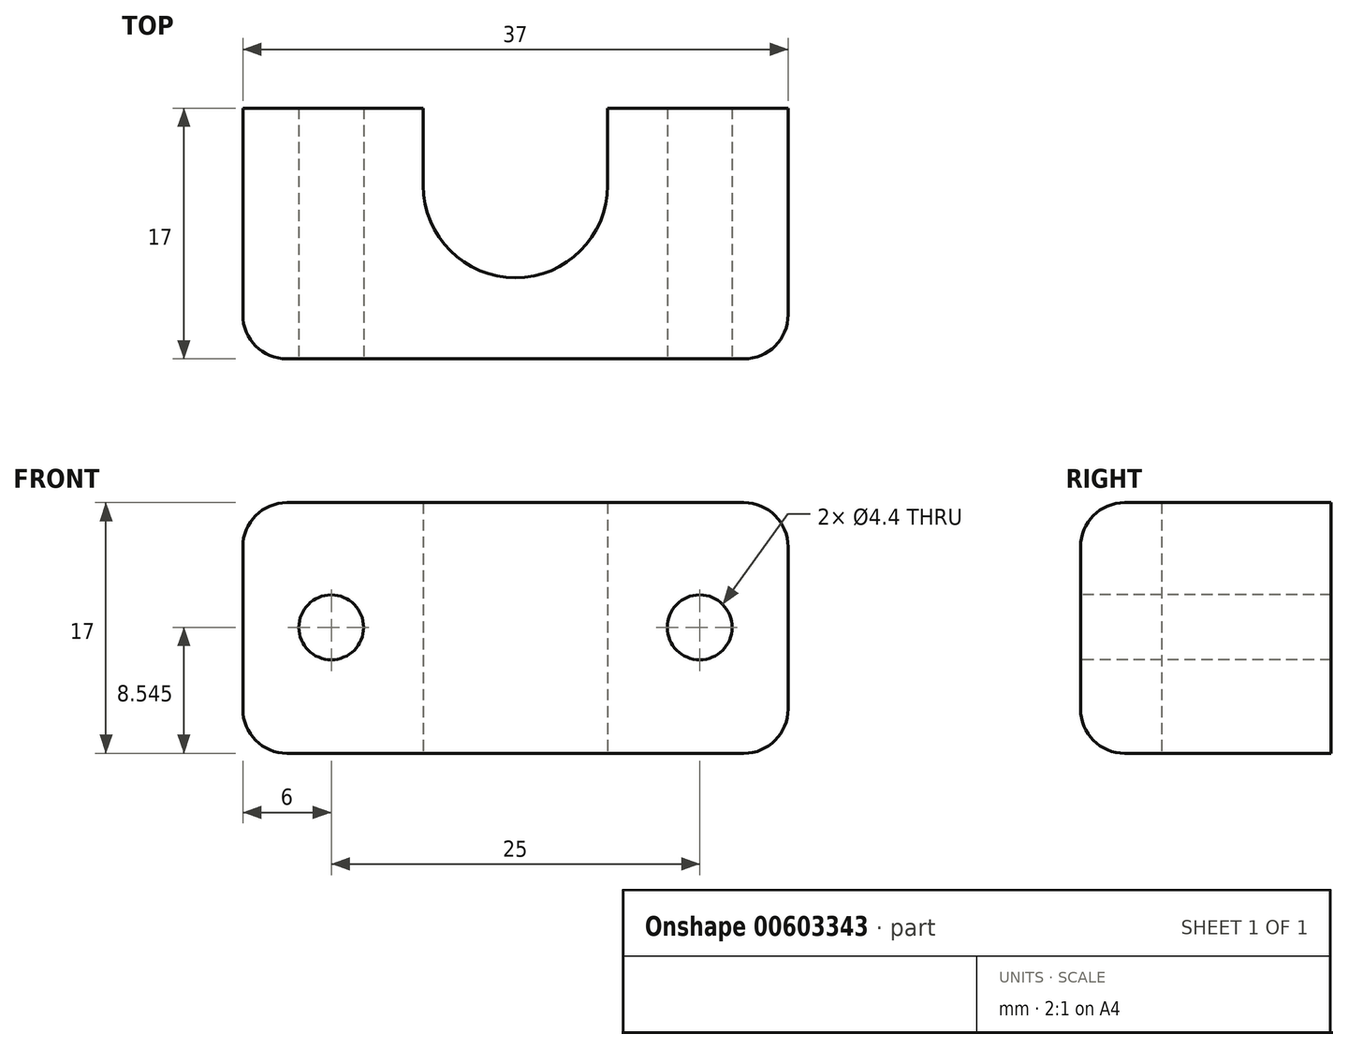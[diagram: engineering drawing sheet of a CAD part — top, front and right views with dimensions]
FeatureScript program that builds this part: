
annotation { "Feature Type Name" : "Feature", "Feature Type Description" : "" }
export const myFeature = defineFeature(function(context is Context, id is Id, definition is map)
    precondition{}
    {
        {
            var Q0;
            Q0=qCreatedBy(makeId("Top.planeOp"),FACE);
            var sketch = newSketch(context, id + "F0", { "sketchPlane" : qUnion([Q0])});
            skLineSegment(sketch, "E0.bottom", {"start": v(0, 0) * mm, "end": v(-37, 0) * mm});
            skLineSegment(sketch, "E0.top", {"start": v(0, 17) * mm, "end": v(-37, 17) * mm});
            skLineSegment(sketch, "E0.left", {"start": v(0, 0) * mm, "end": v(0, 17) * mm});
            skLineSegment(sketch, "E0.right", {"start": v(-37, 0) * mm, "end": v(-37, 17) * mm});
            skCircle(sketch, "E1", {"center": v(-18.5, 11.75) * mm, "radius": 6.25 * mm});
            skLineSegment(sketch, "E2", {"start": v(-18.5, 17) * mm, "end": v(-18.5, 0) * mm, "construction": true});
            skLineSegment(sketch, "E3", {"start": v(-24.75, 11.75) * mm, "end": v(-24.75, 17) * mm});
            skLineSegment(sketch, "E4.MirrorCS", {"start": v(-12.25, 11.75) * mm, "end": v(-12.25, 17) * mm});
            skSolve(sketch);
        }
        {
            var Q0;
            Q0=makeQuery(id+"F0.imprint","IMPRINT",FACE,{"disambiguationData":[TD([[makeQuery(id+"F0.imprint","IMPRINT",EDGE,{"derivedFrom":sQuery(id+"F0.wireOp",EDGE,"E0.bottom")}),-1.0]])]});
            extrude(context, id + "F1", {"entities" : qUnion([Q0]), "depth" : 17 * mm, "offsetDistance" : 25 * mm});
        }
        {
            var Q0;
            Q0=makeQuery(id+"F1.opExtrude","SWEPT_FACE",FACE,{"disambiguationData":[OSD([sQuery(id+"F0.wireOp",EDGE,"E0.bottom")])]});
            var sketch = newSketch(context, id + "F2", { "sketchPlane" : qUnion([Q0])});
            skPoint(sketch, "E5", {"position": v(-6, 8.54) * mm});
            skLineSegment(sketch, "E6", {"start": v(-24.7, 8.68) * mm, "end": v(0, 8.5) * mm, "construction": true});
            skLineSegment(sketch, "E7", {"start": v(-18.5, 17) * mm, "end": v(-18.5, 7.59) * mm, "construction": true});
            skPoint(sketch, "E8.MirrorP", {"position": v(-31, 8.54) * mm});
            skSolve(sketch);
        }
        {
            var Q0;
            Q0=sQuery(id+"F2.wireOp",VERTEX,"E8.MirrorP");
            var Q1;
            Q1=sQuery(id+"F2.wireOp",VERTEX,"E5");
            var Q2;
            Q2=makeQuery(id+"F1.opExtrude","SWEPT_BODY",BODY,{"disambiguationData":[OSD([sQuery(id+"F0.wireOp",EDGE,"E0.bottom"),sQuery(id+"F0.wireOp",EDGE,"E0.top"),sQuery(id+"F0.wireOp",EDGE,"E0.left"),sQuery(id+"F0.wireOp",EDGE,"E0.right"),sQuery(id+"F0.wireOp",EDGE,"E1"),sQuery(id+"F0.wireOp",EDGE,"E3"),sQuery(id+"F0.wireOp",EDGE,"E4.MirrorCS")])]});
            hole(context, id + "F3", {"style" : HoleStyle.SIMPLE, "endStyle" : HoleEndStyle.THROUGH, "standardTappedOrClearance" : lookupTablePath({ "standard" : "ISO", "fit" : "Normal", "size" : "M4", "type" : "Clearance" }), "standardBlindInLast" : lookupTablePath({ "fit" : "Standard", "standard" : "ISO", "size" : "M4", "type" : "Clearance" }), "holeDiameter" : 4.4 * mm, "majorDiameter" : 5 * mm, "isTappedThrough" : true, "tappedDepth" : 12 * mm, "tapClearance" : 3, "locations" : qUnion([Q0, Q1]), "scope" : qUnion([Q2])});
        }
        {
            var Q0;
            Q0=makeQuery(id+"F1.opExtrude","SWEPT_EDGE",EDGE,{"disambiguationData":[OSD([sQuery(id+"F0.wireOp",EDGE,"E0.bottom"),sQuery(id+"F0.wireOp",EDGE,"E0.right")])]});
            var Q1;
            Q1=makeQuery(id+"F1.opExtrude","SWEPT_EDGE",EDGE,{"disambiguationData":[OSD([sQuery(id+"F0.wireOp",EDGE,"E0.bottom"),sQuery(id+"F0.wireOp",EDGE,"E0.left")])]});
            var Q2;
            Q2=makeQuery(id+"F1.opExtrude","CAP_EDGE",EDGE,{"disambiguationData":[OSD([sQuery(id+"F0.wireOp",EDGE,"E0.bottom")])],"isStart":false});
            var Q3;
            Q3=makeQuery(id+"F1.opExtrude","CAP_EDGE",EDGE,{"disambiguationData":[OSD([sQuery(id+"F0.wireOp",EDGE,"E0.bottom")])],"isStart":true});
            var Q4;
            Q4=makeQuery(id+"F1.opExtrude","CAP_EDGE",EDGE,{"disambiguationData":[OSD([sQuery(id+"F0.wireOp",EDGE,"E0.left")])],"isStart":false});
            var Q5;
            Q5=makeQuery(id+"F1.opExtrude","CAP_EDGE",EDGE,{"disambiguationData":[OSD([sQuery(id+"F0.wireOp",EDGE,"E0.left")])],"isStart":true});
            var Q6;
            Q6=makeQuery(id+"F1.opExtrude","CAP_EDGE",EDGE,{"disambiguationData":[OSD([sQuery(id+"F0.wireOp",EDGE,"E0.right")])],"isStart":false});
            var Q7;
            Q7=makeQuery(id+"F1.opExtrude","CAP_EDGE",EDGE,{"disambiguationData":[OSD([sQuery(id+"F0.wireOp",EDGE,"E0.right")])],"isStart":true});
            fillet(context, id + "F4", {"entities" : qUnion([Q0, Q1, Q2, Q3, Q4, Q5, Q6, Q7]), "radius" : 3 * mm, "tangentPropagation" : true, "allowEdgeOverflow" : false});
        }
    });
